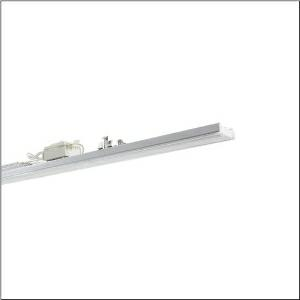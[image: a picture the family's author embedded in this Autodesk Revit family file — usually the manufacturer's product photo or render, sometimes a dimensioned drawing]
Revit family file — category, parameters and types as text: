
# Revit family: licross_r__21_recessed_mo_52tl12dn4axg3s_be2a
name_source: partatom
category: Lighting Fixtures
units: mm (PartAtom-declared; Revit-internal decimal feet)

## family parameters
Cut with Voids When Loaded = No
Host = Face
Light Source = No
Part Type = Normal
Room Calculation Point = No
Round Connector Dimension = Use Diameter
Shared = No

## types (1)
- --- (1 x LED, 950 lm, 6.7 W, 4000K)
    Apparent Load = 7 VA
    CIE Flux Codes = 72 92 99 100 100
    Color Rendering = 80
    Color Temperature = 4000K
    Default Elevation = 1800 mm
    Description = Licross® 21 Recessed MO, luminaire insert, of sheet steel, galvanised, coil coated, white, length: 1.500mm, width: 66mm, height: 67mm, LED rated luminous flux: 10.280lm, light colour: 840, control gear: DALI 2 (for two DALI lines), with plug, 6-pole, with phase selection, for trunking rail, 14-core, mains connection: 220..240V, AC, 50/60Hz, rated input power: 62W, halogen-free wiring, for emergency light function, for trunking rail, 14-core, converter,control gear: single battery element, battery: LiFePO4, 9Ah, primary optical cover: cover, of PMMA, light emission: direct distribution, primary light characteristic: symmetric, protection rating (complete): IP40, insulation class (complete): insulation class I (protective earthing), certification: CE, UKCA, protection symbol: D if used in an environment without relevant dust loads with corresponding accessories, impact resistance: IK06, permissible ambient temperature for indoor applications: +5..+35°C, standard: EN 60598-2-22, LABS conformity tested according to VDMA 24364:2018-05, reducing of maximum allowable ambient temperature of 5°C with ceiling mounting, corresponds to IFS (International Featured Standards) requirements for safety and quality in the food industry, packaging unit: 1 piece
    Height = 58 mm
    Lamp = 1 x LED
    Lamp Light Flux = 950 lm
    Lamp Power = 6.7 W
    Lamp count = 1
    Length = 1500 mm
    Luminous efficacy = 142 lm/W
    Manufacturer = Siteco
    ModVariant = No
    Model = 52TL12DN4AXG3S
    Mounting Place = Ceiling
    Mounting Type = Pendant
    Number of Poles = 1
    OnlyDefault = Yes
    Power Factor = 1
    Product Name = Licross® 21 Recessed MO
    Product group = luminaire insert
    ProductGroupID = 902
    Protection Class = Protection class I
    Protection Degree = IP 40
    RLX_Detail_Level = 1
    RLX_Emergency_Light_Flux = 0 lm
    RLX_Emergency_Type = 0
    RLX_Emergency_Type_DB = No
    RlxData = <blob elided: 25045 chars, md5=3f71ad32>
    Socket = socket
    Standby Power = 0 W
    System Light Flux = 950 lm
    System Power = 7 W
    Type Comments = : emergency light operation: 3 h
    Type Image = l_1296930.jpg
    URL = http://relux.com
    VarID = @adj_110060
    Voltage = 0 V
    Weight = 0.00 kg
    Width = 66 mm

## geometry (parser evidence)
native form markers: Blend x4, Sweep x12
no freeform markers — native parametric forms only
